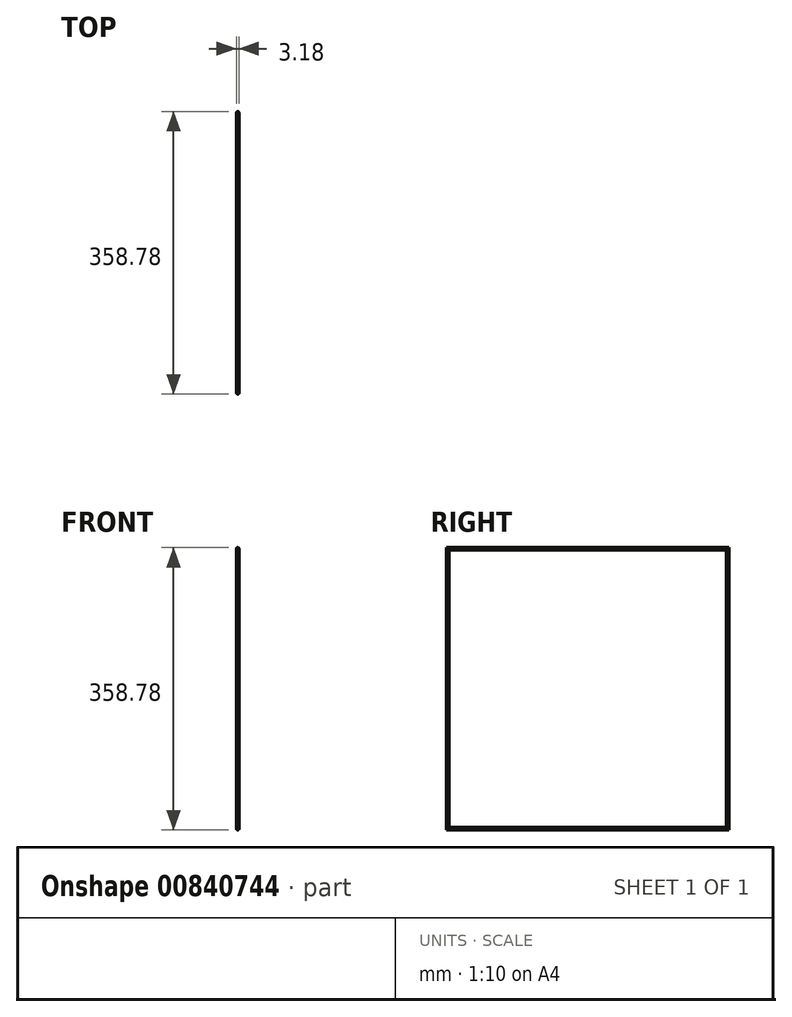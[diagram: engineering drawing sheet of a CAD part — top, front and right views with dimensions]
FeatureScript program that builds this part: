
annotation { "Feature Type Name" : "Feature", "Feature Type Description" : "" }
export const myFeature = defineFeature(function(context is Context, id is Id, definition is map)
    precondition{}
    {
        {
            var Q0;
            Q0=qCreatedBy(makeId("Right.planeOp"),FACE);
            var sketch = newSketch(context, id + "F0", { "sketchPlane" : qUnion([Q0])});
            skLineSegment(sketch, "E0.bottom", {"start": v(0, 0) * mm, "end": v(355.6, 0) * mm});
            skLineSegment(sketch, "E0.top", {"start": v(0, 355.6) * mm, "end": v(355.6, 355.6) * mm});
            skLineSegment(sketch, "E0.left", {"start": v(0, 0) * mm, "end": v(0, 355.6) * mm});
            skLineSegment(sketch, "E0.right", {"start": v(355.6, 0) * mm, "end": v(355.6, 355.6) * mm});
            skSolve(sketch);
        }
        {
            var Q0;
            Q0=qCreatedBy(makeId("Top.planeOp"),FACE);
            var sketch = newSketch(context, id + "F1", { "sketchPlane" : qUnion([Q0])});
            skCircle(sketch, "E1", {"center": v(0, 0) * mm, "radius": 1.59 * mm});
            skSolve(sketch);
        }
        {
            var Q0;
            Q0=makeQuery(id+"F1.imprint","IMPRINT",FACE,{"disambiguationData":[TD([[makeQuery(id+"F1.imprint","IMPRINT",EDGE,{"derivedFrom":sQuery(id+"F1.wireOp",EDGE,"E1")}),1.0]])]});
            var Q1;
            Q1=sQuery(id+"F0.wireOp",EDGE,"E0.left");
            var Q2;
            Q2=sQuery(id+"F0.wireOp",EDGE,"E0.top");
            var Q3;
            Q3=sQuery(id+"F0.wireOp",EDGE,"E0.right");
            var Q4;
            Q4=sQuery(id+"F0.wireOp",EDGE,"E0.bottom");
            sweep(context, id + "F2", {"profiles" : qUnion([Q0]), "path" : qUnion([Q1, Q2, Q3, Q4])});
        }
    });
